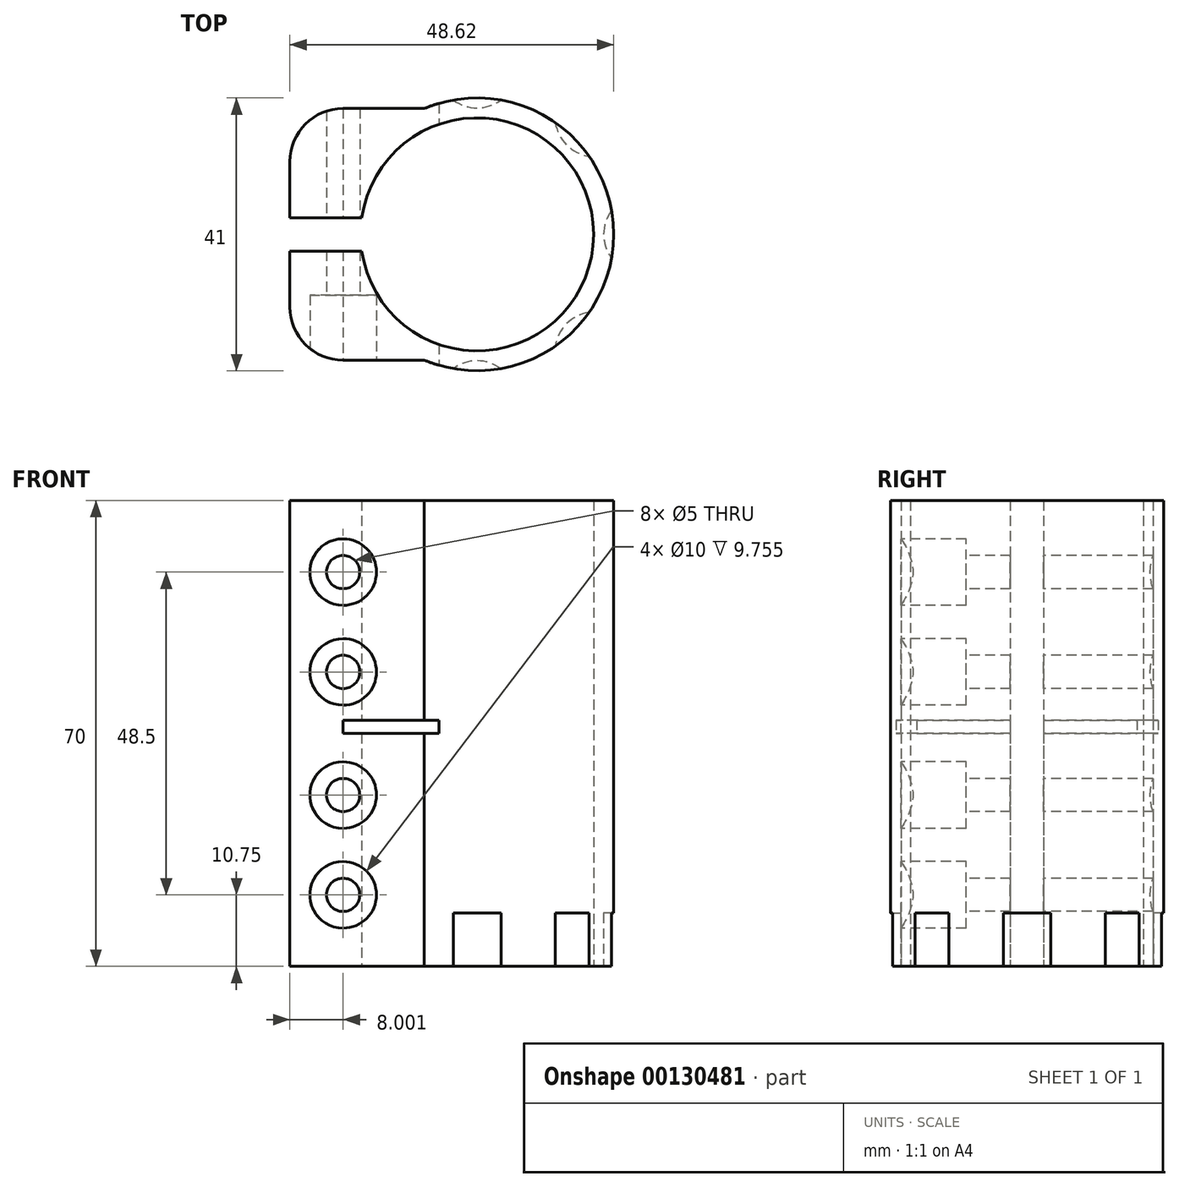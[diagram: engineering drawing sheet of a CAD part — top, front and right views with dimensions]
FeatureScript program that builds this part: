
annotation { "Feature Type Name" : "Feature", "Feature Type Description" : "" }
export const myFeature = defineFeature(function(context is Context, id is Id, definition is map)
    precondition{}
    {
        {
            var Q0;
            Q0=qCreatedBy(makeId("Top.planeOp"),FACE);
            var sketch = newSketch(context, id + "F0", { "sketchPlane" : qUnion([Q0])});
            skArc(sketch, "E0", {"start": v(-17.32, -2.5) * mm, "mid": v(17.5, 0) * mm, "end": v(-17.32, 2.5) * mm});
            skArc(sketch, "E1", {"start": v(-7.92, -18.9) * mm, "mid": v(20.5, 0) * mm, "end": v(-7.92, 18.9) * mm});
            skLineSegment(sketch, "E2", {"start": v(-17.32, 2.5) * mm, "end": v(-28.12, 2.5) * mm});
            skLineSegment(sketch, "E3", {"start": v(-28.12, 2.5) * mm, "end": v(-28.12, 10.9) * mm});
            skLineSegment(sketch, "E4", {"start": v(-20.12, 18.9) * mm, "end": v(-7.92, 18.9) * mm});
            skPoint(sketch, "E5.visualSharp", {"position": v(-28.12, 18.9) * mm});
            skArc(sketch, "E5.filletArc", {"start": v(-20.12, 18.9) * mm, "mid": v(-25.78, 16.57) * mm, "end": v(-28.12, 10.9) * mm});
            skLineSegment(sketch, "E6", {"start": v(0, 0) * mm, "end": v(38.63, 0) * mm, "construction": true});
            skLineSegment(sketch, "E7.MirrorCS", {"start": v(-17.32, -2.5) * mm, "end": v(-28.12, -2.5) * mm});
            skLineSegment(sketch, "E8.MirrorCS", {"start": v(-20.12, -18.9) * mm, "end": v(-7.92, -18.9) * mm});
            skLineSegment(sketch, "E9.MirrorCS", {"start": v(-28.12, -2.5) * mm, "end": v(-28.12, -10.9) * mm});
            skArc(sketch, "E10.MirrorCS", {"start": v(-20.12, -18.9) * mm, "mid": v(-25.78, -16.57) * mm, "end": v(-28.12, -10.9) * mm});
            skSolve(sketch);
        }
        {
            var Q0;
            Q0=makeQuery(id+"F0.imprint","IMPRINT",FACE,{"disambiguationData":[TD([[makeQuery(id+"F0.imprint","IMPRINT",EDGE,{"derivedFrom":sQuery(id+"F0.wireOp",EDGE,"E0")}),-1.0]])]});
            extrude(context, id + "F1", {"entities" : qUnion([Q0]), "depth" : 70 * mm});
        }
        {
            var Q0;
            Q0=makeQuery(id+"F1.opExtrude","SWEPT_FACE",FACE,{"disambiguationData":[OSD([sQuery(id+"F0.wireOp",EDGE,"E8.MirrorCS")])]});
            var sketch = newSketch(context, id + "F2", { "sketchPlane" : qUnion([Q0])});
            skPoint(sketch, "E11", {"position": v(-20.12, 10.75) * mm});
            skPoint(sketch, "E12", {"position": v(-20.12, 25.75) * mm});
            skPoint(sketch, "E13", {"position": v(-20.12, 44.25) * mm});
            skPoint(sketch, "E14", {"position": v(-20.12, 59.25) * mm});
            skPoint(sketch, "E15", {"position": v(0.08, 36) * mm});
            skSolve(sketch);
        }
        {
            var Q0;
            Q0=sQuery(id+"F2.wireOp",VERTEX,"E11");
            var Q1;
            Q1=sQuery(id+"F2.wireOp",VERTEX,"E12");
            var Q2;
            Q2=sQuery(id+"F2.wireOp",VERTEX,"E13");
            var Q3;
            Q3=sQuery(id+"F2.wireOp",VERTEX,"E14");
            var Q4;
            Q4=makeQuery(id+"F1.opExtrude","SWEPT_BODY",BODY,{"disambiguationData":[OSD([sQuery(id+"F0.wireOp",EDGE,"E0"),sQuery(id+"F0.wireOp",EDGE,"E1"),sQuery(id+"F0.wireOp",EDGE,"E2"),sQuery(id+"F0.wireOp",EDGE,"E3"),sQuery(id+"F0.wireOp",EDGE,"E4"),sQuery(id+"F0.wireOp",EDGE,"E5.filletArc"),sQuery(id+"F0.wireOp",EDGE,"E7.MirrorCS"),sQuery(id+"F0.wireOp",EDGE,"E8.MirrorCS"),sQuery(id+"F0.wireOp",EDGE,"E9.MirrorCS"),sQuery(id+"F0.wireOp",EDGE,"E10.MirrorCS")])]});
            hole(context, id + "F3", {"style" : HoleStyle.C_BORE, "endStyle" : HoleEndStyle.THROUGH, "holeDiameter" : 5 * mm, "cBoreDiameter" : 10 * mm, "cBoreDepth" : 8 * mm, "locations" : qUnion([Q0, Q1, Q2, Q3]), "scope" : qUnion([Q4]), "isTappedThrough" : true});
        }
        {
            var Q0;
            Q0=qCreatedBy(makeId("Front.planeOp"),FACE);
            var sketch = newSketch(context, id + "F4", { "sketchPlane" : qUnion([Q0])});
            skArc(sketch, "E16.0.0", {"start": v(-20.12, 64.25) * mm, "mid": v(-15.12, 59.25) * mm, "end": v(-20.12, 54.25) * mm});
            skLineSegment(sketch, "E16.0.1", {"start": v(-20.12, 54.25) * mm, "end": v(-20.12, 49.25) * mm});
            skArc(sketch, "E16.0.2", {"start": v(-20.12, 49.25) * mm, "mid": v(-15.12, 44.25) * mm, "end": v(-20.12, 39.25) * mm});
            skLineSegment(sketch, "E16.0.3", {"start": v(-20.12, 39.25) * mm, "end": v(-20.12, 30.75) * mm});
            skArc(sketch, "E16.0.4", {"start": v(-20.12, 30.75) * mm, "mid": v(-15.12, 25.75) * mm, "end": v(-20.12, 20.75) * mm});
            skLineSegment(sketch, "E16.0.5", {"start": v(-20.12, 20.75) * mm, "end": v(-20.12, 15.75) * mm});
            skArc(sketch, "E16.0.6", {"start": v(-20.12, 15.75) * mm, "mid": v(-15.12, 10.75) * mm, "end": v(-20.12, 5.75) * mm});
            skLineSegment(sketch, "E16.0.7", {"start": v(-20.12, 5.75) * mm, "end": v(-20.12, 0) * mm});
            skLineSegment(sketch, "E16.0.8", {"start": v(-20.12, 0) * mm, "end": v(-7.92, 0) * mm});
            skLineSegment(sketch, "E16.0.9", {"start": v(-7.92, 0) * mm, "end": v(-7.92, 70) * mm});
            skLineSegment(sketch, "E16.0.10", {"start": v(-7.92, 70) * mm, "end": v(-20.12, 70) * mm});
            skLineSegment(sketch, "E16.0.11", {"start": v(-20.12, 70) * mm, "end": v(-20.12, 64.25) * mm});
            skLineSegment(sketch, "E17.0.0", {"start": v(-20.12, 49.25) * mm, "end": v(-20.12, 54.25) * mm});
            skArc(sketch, "E17.0.1", {"start": v(-20.12, 64.25) * mm, "mid": v(-25.12, 59.25) * mm, "end": v(-20.12, 54.25) * mm});
            skLineSegment(sketch, "E17.0.2", {"start": v(-20.12, 64.25) * mm, "end": v(-20.12, 70) * mm});
            skLineSegment(sketch, "E17.0.3", {"start": v(-20.12, 70) * mm, "end": v(-28.12, 70) * mm});
            skLineSegment(sketch, "E17.0.4", {"start": v(-28.12, 70) * mm, "end": v(-28.12, 0) * mm});
            skLineSegment(sketch, "E17.0.5", {"start": v(-28.12, 0) * mm, "end": v(-20.12, 0) * mm});
            skLineSegment(sketch, "E17.0.6", {"start": v(-20.12, 0) * mm, "end": v(-20.12, 5.75) * mm});
            skArc(sketch, "E17.0.7", {"start": v(-20.12, 15.75) * mm, "mid": v(-25.12, 10.75) * mm, "end": v(-20.12, 5.75) * mm});
            skLineSegment(sketch, "E17.0.8", {"start": v(-20.12, 15.75) * mm, "end": v(-20.12, 20.75) * mm});
            skArc(sketch, "E17.0.9", {"start": v(-20.12, 30.75) * mm, "mid": v(-25.12, 25.75) * mm, "end": v(-20.12, 20.75) * mm});
            skLineSegment(sketch, "E17.0.10", {"start": v(-20.12, 30.75) * mm, "end": v(-20.12, 39.25) * mm});
            skArc(sketch, "E17.0.11", {"start": v(-20.12, 49.25) * mm, "mid": v(-25.12, 44.25) * mm, "end": v(-20.12, 39.25) * mm});
            skLineSegment(sketch, "E18.bottom", {"start": v(-28.12, 37) * mm, "end": v(-5.72, 37) * mm});
            skLineSegment(sketch, "E18.top", {"start": v(-28.12, 35) * mm, "end": v(-5.72, 35) * mm});
            skLineSegment(sketch, "E18.left", {"start": v(-28.12, 37) * mm, "end": v(-28.12, 35) * mm});
            skLineSegment(sketch, "E18.right", {"start": v(-5.72, 37) * mm, "end": v(-5.72, 35) * mm});
            skSolve(sketch);
        }
        {
            var Q0;
            {var subQ5=sQuery(id+"F4.wireOp",EDGE,"E18.left");Q0=makeQuery(id+"F4.imprint","IMPRINT",FACE,{"disambiguationData":[TD([[makeQuery(id+"F4.imprint","IMPRINT",EDGE,{"derivedFrom":subQ5}),1.0]])]});}
            var Q1;
            {var subQ0=sQuery(id+"F4.wireOp",EDGE,"E18.top");var subQ1=sQuery(id+"F4.wireOp",EDGE,"E16.0.9");var subQ2=makeQuery(id+"F4.imprint","INTERSECT",VERTEX,{"derivedFrom":[subQ1,subQ0]});Q1=makeQuery(id+"F4.imprint","IMPRINT",FACE,{"disambiguationData":[TD([[makeQuery(id+"F4.imprint","IMPRINT",EDGE,{"disambiguationData":[TD([[subQ2,-1.0]])],"derivedFrom":subQ1}),1.0]])]});}
            var Q2;
            {var subQ5=sQuery(id+"F4.wireOp",EDGE,"E18.right");Q2=makeQuery(id+"F4.imprint","IMPRINT",FACE,{"disambiguationData":[TD([[makeQuery(id+"F4.imprint","IMPRINT",EDGE,{"derivedFrom":subQ5}),-1.0]])]});}
            extrude(context, id + "F5", {"entities" : qUnion([Q0, Q1, Q2]), "operationType" : NewBodyOperationType.REMOVE, "endBound" : BoundingType.SYMMETRIC, "oppositeDirection" : true, "depth" : 50 * mm});
        }
        {
            var Q0;
            Q0=makeQuery(id+"F1.opExtrude","CAP_FACE",FACE,{"disambiguationData":[OSD([sQuery(id+"F0.wireOp",EDGE,"E0"),sQuery(id+"F0.wireOp",EDGE,"E1"),sQuery(id+"F0.wireOp",EDGE,"E2"),sQuery(id+"F0.wireOp",EDGE,"E3"),sQuery(id+"F0.wireOp",EDGE,"E4"),sQuery(id+"F0.wireOp",EDGE,"E5.filletArc"),sQuery(id+"F0.wireOp",EDGE,"E7.MirrorCS"),sQuery(id+"F0.wireOp",EDGE,"E8.MirrorCS"),sQuery(id+"F0.wireOp",EDGE,"E9.MirrorCS"),sQuery(id+"F0.wireOp",EDGE,"E10.MirrorCS")])],"isStart":true});
            var sketch = newSketch(context, id + "F6", { "sketchPlane" : qUnion([Q0])});
            skCircle(sketch, "E19", {"center": v(0, -25) * mm, "radius": 6 * mm});
            skCircle(sketch, "E20.1.0", {"center": v(17.68, -17.68) * mm, "radius": 6 * mm});
            skCircle(sketch, "E20.2.0", {"center": v(25, 0) * mm, "radius": 6 * mm});
            skCircle(sketch, "E20.3.0", {"center": v(17.68, 17.68) * mm, "radius": 6 * mm});
            skCircle(sketch, "E20.4.0", {"center": v(0, 25) * mm, "radius": 6 * mm});
            skPoint(sketch, "E20.center", {"position": v(0, 0) * mm});
            skLineSegment(sketch, "E20.anchor1", {"start": v(0, 0) * mm, "end": v(0, -25) * mm, "construction": true});
            skLineSegment(sketch, "E20.anchor2", {"start": v(0, 0) * mm, "end": v(0, 25) * mm, "construction": true});
            skSolve(sketch);
        }
        {
            var Q0;
            {var subQ0=sQuery(id+"F6.wireOp",EDGE,"E19");var subQ1=makeQuery(id+"F1.opExtrude","CAP_EDGE",EDGE,{"disambiguationData":[OSD([sQuery(id+"F0.wireOp",EDGE,"E1")])],"isStart":true});var subQ2=makeQuery(id+"F6.imprint","INTERSECT",VERTEX,{"disambiguationData":[OD(0.0)],"derivedFrom":[subQ1,subQ0]});Q0=makeQuery(id+"F6.imprint","IMPRINT",FACE,{"disambiguationData":[TD([[makeQuery(id+"F6.imprint","IMPRINT",EDGE,{"disambiguationData":[TD([[subQ2,-1.0]])],"derivedFrom":subQ0}),1.0]])]});}
            var Q1;
            {var subQ0=sQuery(id+"F6.wireOp",EDGE,"E20.1.0");var subQ1=makeQuery(id+"F1.opExtrude","CAP_EDGE",EDGE,{"disambiguationData":[OSD([sQuery(id+"F0.wireOp",EDGE,"E1")])],"isStart":true});var subQ2=makeQuery(id+"F6.imprint","INTERSECT",VERTEX,{"disambiguationData":[OD(0.0)],"derivedFrom":[subQ1,subQ0]});Q1=makeQuery(id+"F6.imprint","IMPRINT",FACE,{"disambiguationData":[TD([[makeQuery(id+"F6.imprint","IMPRINT",EDGE,{"disambiguationData":[TD([[subQ2,-1.0]])],"derivedFrom":subQ0}),1.0]])]});}
            var Q2;
            {var subQ0=sQuery(id+"F6.wireOp",EDGE,"E20.3.0");var subQ1=makeQuery(id+"F1.opExtrude","CAP_EDGE",EDGE,{"disambiguationData":[OSD([sQuery(id+"F0.wireOp",EDGE,"E1")])],"isStart":true});var subQ2=makeQuery(id+"F6.imprint","INTERSECT",VERTEX,{"disambiguationData":[OD(0.0)],"derivedFrom":[subQ1,subQ0]});Q2=makeQuery(id+"F6.imprint","IMPRINT",FACE,{"disambiguationData":[TD([[makeQuery(id+"F6.imprint","IMPRINT",EDGE,{"disambiguationData":[TD([[subQ2,1.0]])],"derivedFrom":subQ0}),1.0]])]});}
            var Q3;
            {var subQ0=sQuery(id+"F6.wireOp",EDGE,"E20.4.0");var subQ1=makeQuery(id+"F1.opExtrude","CAP_EDGE",EDGE,{"disambiguationData":[OSD([sQuery(id+"F0.wireOp",EDGE,"E1")])],"isStart":true});var subQ2=makeQuery(id+"F6.imprint","INTERSECT",VERTEX,{"disambiguationData":[OD(0.0)],"derivedFrom":[subQ1,subQ0]});Q3=makeQuery(id+"F6.imprint","IMPRINT",FACE,{"disambiguationData":[TD([[makeQuery(id+"F6.imprint","IMPRINT",EDGE,{"disambiguationData":[TD([[subQ2,1.0]])],"derivedFrom":subQ0}),1.0]])]});}
            var Q4;
            {var subQ0=sQuery(id+"F6.wireOp",EDGE,"E20.4.0");var subQ1=makeQuery(id+"F1.opExtrude","CAP_EDGE",EDGE,{"disambiguationData":[OSD([sQuery(id+"F0.wireOp",EDGE,"E1")])],"isStart":true});var subQ2=makeQuery(id+"F6.imprint","INTERSECT",VERTEX,{"disambiguationData":[OD(0.0)],"derivedFrom":[subQ1,subQ0]});Q4=makeQuery(id+"F6.imprint","IMPRINT",FACE,{"disambiguationData":[TD([[makeQuery(id+"F6.imprint","IMPRINT",EDGE,{"disambiguationData":[TD([[subQ2,-1.0]])],"derivedFrom":subQ0}),1.0]])]});}
            var Q5;
            {var subQ0=sQuery(id+"F6.wireOp",EDGE,"E20.3.0");var subQ1=makeQuery(id+"F1.opExtrude","CAP_EDGE",EDGE,{"disambiguationData":[OSD([sQuery(id+"F0.wireOp",EDGE,"E1")])],"isStart":true});var subQ2=makeQuery(id+"F6.imprint","INTERSECT",VERTEX,{"disambiguationData":[OD(0.0)],"derivedFrom":[subQ1,subQ0]});Q5=makeQuery(id+"F6.imprint","IMPRINT",FACE,{"disambiguationData":[TD([[makeQuery(id+"F6.imprint","IMPRINT",EDGE,{"disambiguationData":[TD([[subQ2,-1.0]])],"derivedFrom":subQ0}),1.0]])]});}
            var Q6;
            {var subQ0=sQuery(id+"F6.wireOp",EDGE,"E20.2.0");var subQ1=makeQuery(id+"F1.opExtrude","CAP_EDGE",EDGE,{"disambiguationData":[OSD([sQuery(id+"F0.wireOp",EDGE,"E1")])],"isStart":true});var subQ2=makeQuery(id+"F6.imprint","INTERSECT",VERTEX,{"disambiguationData":[OD(0.0)],"derivedFrom":[subQ1,subQ0]});Q6=makeQuery(id+"F6.imprint","IMPRINT",FACE,{"disambiguationData":[TD([[makeQuery(id+"F6.imprint","IMPRINT",EDGE,{"disambiguationData":[TD([[subQ2,1.0]])],"derivedFrom":subQ0}),1.0]])]});}
            var Q7;
            {var subQ0=sQuery(id+"F6.wireOp",EDGE,"E20.1.0");var subQ1=makeQuery(id+"F1.opExtrude","CAP_EDGE",EDGE,{"disambiguationData":[OSD([sQuery(id+"F0.wireOp",EDGE,"E1")])],"isStart":true});var subQ2=makeQuery(id+"F6.imprint","INTERSECT",VERTEX,{"disambiguationData":[OD(0.0)],"derivedFrom":[subQ1,subQ0]});Q7=makeQuery(id+"F6.imprint","IMPRINT",FACE,{"disambiguationData":[TD([[makeQuery(id+"F6.imprint","IMPRINT",EDGE,{"disambiguationData":[TD([[subQ2,1.0]])],"derivedFrom":subQ0}),1.0]])]});}
            var Q8;
            {var subQ0=sQuery(id+"F6.wireOp",EDGE,"E20.2.0");var subQ1=makeQuery(id+"F1.opExtrude","CAP_EDGE",EDGE,{"disambiguationData":[OSD([sQuery(id+"F0.wireOp",EDGE,"E1")])],"isStart":true});var subQ2=makeQuery(id+"F6.imprint","INTERSECT",VERTEX,{"disambiguationData":[OD(0.0)],"derivedFrom":[subQ1,subQ0]});Q8=makeQuery(id+"F6.imprint","IMPRINT",FACE,{"disambiguationData":[TD([[makeQuery(id+"F6.imprint","IMPRINT",EDGE,{"disambiguationData":[TD([[subQ2,-1.0]])],"derivedFrom":subQ0}),1.0]])]});}
            var Q9;
            {var subQ0=sQuery(id+"F6.wireOp",EDGE,"E19");var subQ1=makeQuery(id+"F1.opExtrude","CAP_EDGE",EDGE,{"disambiguationData":[OSD([sQuery(id+"F0.wireOp",EDGE,"E1")])],"isStart":true});var subQ2=makeQuery(id+"F6.imprint","INTERSECT",VERTEX,{"disambiguationData":[OD(0.0)],"derivedFrom":[subQ1,subQ0]});Q9=makeQuery(id+"F6.imprint","IMPRINT",FACE,{"disambiguationData":[TD([[makeQuery(id+"F6.imprint","IMPRINT",EDGE,{"disambiguationData":[TD([[subQ2,1.0]])],"derivedFrom":subQ0}),1.0]])]});}
            extrude(context, id + "F7", {"entities" : qUnion([Q0, Q1, Q2, Q3, Q4, Q5, Q6, Q7, Q8, Q9]), "operationType" : NewBodyOperationType.REMOVE, "oppositeDirection" : true, "depth" : 8 * mm});
        }
    });
